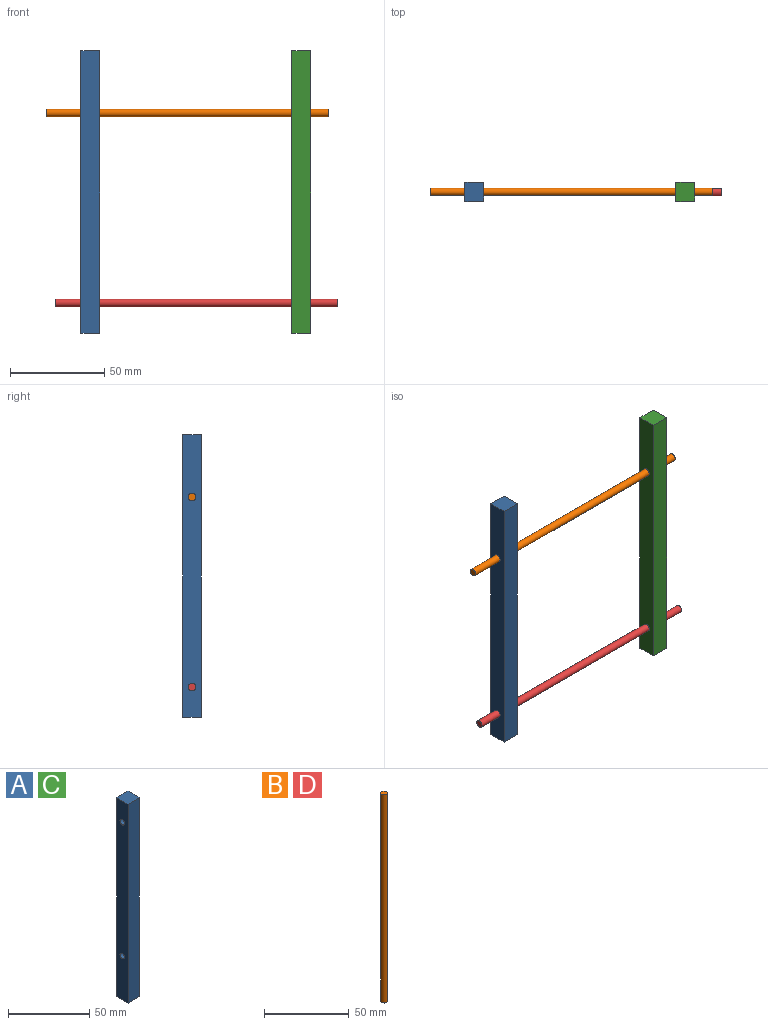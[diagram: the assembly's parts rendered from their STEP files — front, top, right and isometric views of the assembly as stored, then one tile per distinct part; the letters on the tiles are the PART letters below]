
ASSEMBLY  parts=4 mates=4
PART A: 8 faces, bbox 10x10x150 mm
  f0: plane 150x10mm, normal (0,-1,0), area 1500mm2, adj f1,f3,f4,f5
  f1: plane 150x10mm, normal (1,0,0), area 1474.9mm2, adj f0,f2,f4,f5,f6,f7
  f2: plane 150x10mm, normal (0,1,0), area 1500mm2, adj f1,f3,f4,f5
  f3: plane 150x10mm, normal (-1,0,0), area 1474.9mm2, adj f0,f2,f4,f5,f6,f7
  f4: plane 10x10mm, normal (0,0,1), area 100mm2, adj f0,f1,f2,f3
  f5: plane 10x10mm, normal (0,0,-1), area 100mm2, adj f0,f1,f2,f3
  f6: cylinder r=2mm len=10mm, axis (-1,0,0), area 125.7mm2, adj f1,f3
  f7: cylinder r=2mm len=10mm, axis (-1,0,0), area 125.7mm2, adj f1,f3
PART B: 3 faces, bbox 4x4x150 mm
  f0: cylinder r=2mm len=150mm, axis (0,0,-1), area 1885mm2, adj f1,f2
  f1: plane 4x4mm, normal (0,0,1), area 12.6mm2, adj f0
  f2: plane 4x4mm, normal (0,0,-1), area 12.6mm2, adj f0
PART C: same geometry as A
PART D: same geometry as B
PLACE A rot(axis=(0,1,0),180deg) t=(-61.29,34.39,-27.94)mm
PLACE B rot(axis=(0,1,0),90deg) t=(-84.67,34.39,-60.94)mm
PLACE C rot(axis=(0,1,0),180deg) t=(50.78,34.39,-27.94)mm
PLACE D rot(axis=(0.71,0,-0.71),180deg) t=(70.17,34.39,-161.94)mm
MATE slider D.f0 <-> C.f7  axis (1,0,0) through (70.17,34.39,-161.94)mm
MATE slider D.f0 <-> A.f7  axis (-1,0,0) through (-79.83,34.39,-161.94)mm
MATE slider C.f6 <-> B.f0  axis (1,0,0) through (45.78,34.39,-60.94)mm
MATE slider B.f0 <-> A.f6  axis (-1,0,0) through (-84.67,34.39,-60.94)mm
